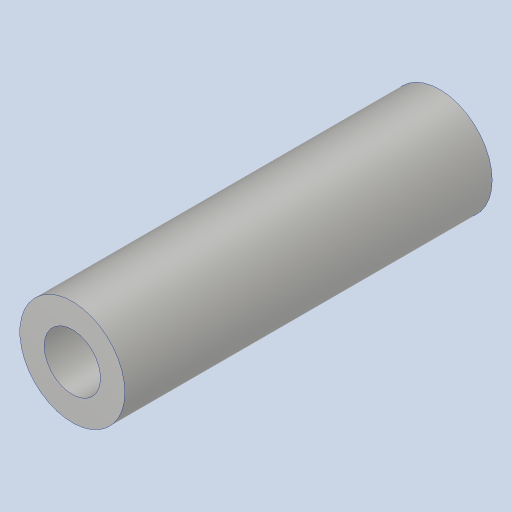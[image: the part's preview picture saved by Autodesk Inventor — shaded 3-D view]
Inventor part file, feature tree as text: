
AUTODESK INVENTOR PART (.ipt)
format: ipt  version: 2023.4 (Build 274418000, 418)  size: 116,736 bytes
history: native  units: in
note: dims shown in document units (in); Inventor stores cm internally (conversion verified against a paired STEP export)
features: extrude x1, hole x1
ambient origin geometry x8: Origin, YZ Plane, XZ Plane, XY Plane, X Axis, Y Axis, Z Axis, Center Point
bodies: Solid1 (feature_tree)
feature tree (2):
  extrude  "Extrusion1"  Depth=1.311in
  hole  "Hole1"  [1 undecoded]
note: 1 required parameter value undecoded (feature->parameter linkage not recoverable at this tier; creation-order binding heuristic only, values carry confidence <= 0.55)
